# Revit family: RN 84234 Optiflex-Flowpress-Übergang
name_source: partatom
category: Rohrformteile
units: mm (PartAtom-declared; Revit-internal decimal feet)

## family parameters
Arbeitsebenenbasiert = Nein
Beim Laden mit Abzugskörper schneiden = Nein
Bemaßung runder Anschluss = Durchmesser verwenden
Gemeinsam genutzt = Nein
Immer vertikal = Ja
Teiletyp = Verbindung

## types (8) — shared parameters
1.010.00.2 Blattnummer der Richtlinie = 29
1.010.00.3 Ausgabedatum (Monat) der Richtlinie = 201308
1.010.00.4 Herstellername = R. Nussbaum AG
1.010.00.5 Revisionsdatum der Datei = 20190521
1.010.00.6 Webadresse des Herstellers = http://www.nussbaum.ch
1.100.00.4 Produktbezeichnung = Versorgung
1.110.00.2 Index = 5
1.110.00.4 Produktbezeichnung = Optiflex
1.960/3L.00.8 Link (URL) = https://www.nussbaum.ch
29.700.00.4 Produktname = Optiflex-Flowpress-Übergang, auf Optipress-Aquaplus, mit Einsteckende
29.700.00.5 Produktkennung = 2
29.700.00.6 Querschnittsform = 1
29.700.00.7 Nennweitensystem = DN
29.700.00.8 Nenndrucksystem = PN
29.710.02.4 Nenndruck = 10
29.710.02.5 max. zul. Überdruck [hPa] = 1000
29.710.02.7 max. zul. Dauer-Betriebsdruck [hPa] = 1000
29.710.02.9 max. zul. Dauer-Betriebstemperatur [°C] = 70
Connector Visibility = Nein
EnclosingSpace Visibility = Nein
Hersteller = R. Nussbaum AG
URL = https://www.nussbaum.ch

## per-type parameters (varying)
- DN=40: 1.800.00.3 TGA-Nummer=01900500000000000000000000000000000000000000000019000000000000000008; 1.800.00.4 Kommentarfeld=84234.28, Optiflex-Flowpress-Übergang, auf Optipress-Aquaplus, mit Einsteckende, DN=40, L=88; 1.810.00.3 Hersteller-Bestellnummer=84234.28; 1.810.00.4 DATANORM-Nummer=84234.28; 1.810.00.6 GTIN-Nummer=7612945744821; 29.710.02.10 Formstück-Gewicht [kg]=0.316; 29.710.02.3 Benennung=Optiflex-Flowpress-Übergang, auf Optipress-Aquaplus, mit Einsteckende, DN=40, L=88; CONNECTOR0_DIAMETER_dX_0r=40 mm; CONNECTOR0_dX_01=26 mm; CONNECTOR0_ref_dX=26 mm; CONNECTOR1_DIAMETER_dX_0r=40 mm; CONNECTOR1_dX_00=53 mm; CONNECTOR1_dX_01=89 mm; CONNECTOR1_ref_dX=89 mm; Modell=84234.28; R. Nussbaum AG 84234.21 de Visibility=Nein; R. Nussbaum AG 84234.22 de Visibility=Nein; R. Nussbaum AG 84234.23 de Visibility=Nein; R. Nussbaum AG 84234.24 de Visibility=Nein; R. Nussbaum AG 84234.25 de Visibility=Nein; R. Nussbaum AG 84234.26 de Visibility=Nein; R. Nussbaum AG 84234.27 de Visibility=Nein; R. Nussbaum AG 84234.28 de Visibility=Ja; Typenkommentare=Optiflex-Flowpress-Übergang DN=40
- DN=32: 1.800.00.3 TGA-Nummer=01900500000000000000000000000000000000000000000019000000000000000007; 1.800.00.4 Kommentarfeld=84234.27, Optiflex-Flowpress-Übergang, auf Optipress-Aquaplus, mit Einsteckende, DN=32, L=74; 1.810.00.3 Hersteller-Bestellnummer=84234.27; 1.810.00.4 DATANORM-Nummer=84234.27; 1.810.00.6 GTIN-Nummer=7612945730848; 29.710.02.10 Formstück-Gewicht [kg]=0.219; 29.710.02.3 Benennung=Optiflex-Flowpress-Übergang, auf Optipress-Aquaplus, mit Einsteckende, DN=32, L=74; CONNECTOR0_DIAMETER_dX_0r=32 mm; CONNECTOR0_dX_01=26 mm; CONNECTOR0_ref_dX=26 mm; CONNECTOR1_DIAMETER_dX_0r=32 mm; CONNECTOR1_dX_00=47 mm; CONNECTOR1_dX_01=73 mm; CONNECTOR1_ref_dX=73 mm; Modell=84234.27; R. Nussbaum AG 84234.21 de Visibility=Nein; R. Nussbaum AG 84234.22 de Visibility=Nein; R. Nussbaum AG 84234.23 de Visibility=Nein; R. Nussbaum AG 84234.24 de Visibility=Nein; R. Nussbaum AG 84234.25 de Visibility=Nein; R. Nussbaum AG 84234.26 de Visibility=Nein; R. Nussbaum AG 84234.27 de Visibility=Ja; R. Nussbaum AG 84234.28 de Visibility=Nein; Typenkommentare=Optiflex-Flowpress-Übergang DN=32
- DN=25: 1.800.00.3 TGA-Nummer=01900500000000000000000000000000000000000000000019000000000000000006; 1.800.00.4 Kommentarfeld=84234.26, Optiflex-Flowpress-Übergang, auf Optipress-Aquaplus, mit Einsteckende, DN=25, L=61; 1.810.00.3 Hersteller-Bestellnummer=84234.26; 1.810.00.4 DATANORM-Nummer=84234.26; 1.810.00.5 StLB-Nummer=346.474; 1.810.00.6 GTIN-Nummer=7612945730831; 29.710.02.10 Formstück-Gewicht [kg]=0.116; 29.710.02.3 Benennung=Optiflex-Flowpress-Übergang, auf Optipress-Aquaplus, mit Einsteckende, DN=25, L=61; CONNECTOR0_DIAMETER_dX_0r=25 mm  [stored 0.082021 ft]; CONNECTOR0_dX_01=20 mm; CONNECTOR0_ref_dX=20 mm; CONNECTOR1_DIAMETER_dX_0r=25 mm  [stored 0.082021 ft]; CONNECTOR1_dX_00=37 mm; CONNECTOR1_dX_01=61 mm; CONNECTOR1_ref_dX=61 mm; Modell=84234.26; R. Nussbaum AG 84234.21 de Visibility=Nein; R. Nussbaum AG 84234.22 de Visibility=Nein; R. Nussbaum AG 84234.23 de Visibility=Nein; R. Nussbaum AG 84234.24 de Visibility=Nein; R. Nussbaum AG 84234.25 de Visibility=Nein; R. Nussbaum AG 84234.26 de Visibility=Ja; R. Nussbaum AG 84234.27 de Visibility=Nein; R. Nussbaum AG 84234.28 de Visibility=Nein; Typenkommentare=Optiflex-Flowpress-Übergang DN=25
- DN=20: 1.800.00.3 TGA-Nummer=01900500000000000000000000000000000000000000000019000000000000000005; 1.800.00.4 Kommentarfeld=84234.25, Optiflex-Flowpress-Übergang, auf Optipress-Aquaplus, mit Einsteckende, DN=20, L=60; 1.810.00.3 Hersteller-Bestellnummer=84234.25; 1.810.00.4 DATANORM-Nummer=84234.25; 1.810.00.5 StLB-Nummer=346.473; 1.810.00.6 GTIN-Nummer=7612945730824; 29.710.02.10 Formstück-Gewicht [kg]=0.078; 29.710.02.3 Benennung=Optiflex-Flowpress-Übergang, auf Optipress-Aquaplus, mit Einsteckende, DN=20, L=60; CONNECTOR0_DIAMETER_dX_0r=20 mm; CONNECTOR0_dX_01=20 mm; CONNECTOR0_ref_dX=20 mm; CONNECTOR1_DIAMETER_dX_0r=20 mm; CONNECTOR1_dX_00=36 mm; CONNECTOR1_dX_01=60 mm; CONNECTOR1_ref_dX=60 mm; Modell=84234.25; R. Nussbaum AG 84234.21 de Visibility=Nein; R. Nussbaum AG 84234.22 de Visibility=Nein; R. Nussbaum AG 84234.23 de Visibility=Nein; R. Nussbaum AG 84234.24 de Visibility=Nein; R. Nussbaum AG 84234.25 de Visibility=Ja; R. Nussbaum AG 84234.26 de Visibility=Nein; R. Nussbaum AG 84234.27 de Visibility=Nein; R. Nussbaum AG 84234.28 de Visibility=Nein; Typenkommentare=Optiflex-Flowpress-Übergang DN=20
- DN=15x20: 1.800.00.3 TGA-Nummer=01900500000000000000000000000000000000000000000019000000000000000004; 1.800.00.4 Kommentarfeld=84234.24, Optiflex-Flowpress-Übergang, auf Optipress-Aquaplus, mit Einsteckende, DN=15x20, L=54; 1.810.00.3 Hersteller-Bestellnummer=84234.24; 1.810.00.4 DATANORM-Nummer=84234.24; 1.810.00.5 StLB-Nummer=346.472; 1.810.00.6 GTIN-Nummer=7612945730817; 29.710.02.10 Formstück-Gewicht [kg]=0.05; 29.710.02.3 Benennung=Optiflex-Flowpress-Übergang, auf Optipress-Aquaplus, mit Einsteckende, DN=15x20, L=54; CONNECTOR0_DIAMETER_dX_0r=15 mm; CONNECTOR0_dX_01=14 mm  [stored 0.0459318 ft]; CONNECTOR0_ref_dX=14 mm  [stored 0.0459318 ft]; CONNECTOR1_DIAMETER_dX_0r=20 mm; CONNECTOR1_dX_00=30 mm; CONNECTOR1_dX_01=54 mm; CONNECTOR1_ref_dX=54 mm; Modell=84234.24; R. Nussbaum AG 84234.21 de Visibility=Nein; R. Nussbaum AG 84234.22 de Visibility=Nein; R. Nussbaum AG 84234.23 de Visibility=Nein; R. Nussbaum AG 84234.24 de Visibility=Ja; R. Nussbaum AG 84234.25 de Visibility=Nein; R. Nussbaum AG 84234.26 de Visibility=Nein; R. Nussbaum AG 84234.27 de Visibility=Nein; R. Nussbaum AG 84234.28 de Visibility=Nein; Typenkommentare=Optiflex-Flowpress-Übergang DN=15x20
- DN=15: 1.800.00.3 TGA-Nummer=01900500000000000000000000000000000000000000000019000000000000000003; 1.800.00.4 Kommentarfeld=84234.23, Optiflex-Flowpress-Übergang, auf Optipress-Aquaplus, mit Einsteckende, DN=15, L=51; 1.810.00.3 Hersteller-Bestellnummer=84234.23; 1.810.00.4 DATANORM-Nummer=84234.23; 1.810.00.5 StLB-Nummer=346.472; 1.810.00.6 GTIN-Nummer=7612945730800; 29.710.02.10 Formstück-Gewicht [kg]=0.041; 29.710.02.3 Benennung=Optiflex-Flowpress-Übergang, auf Optipress-Aquaplus, mit Einsteckende, DN=15, L=51; CONNECTOR0_DIAMETER_dX_0r=15 mm; CONNECTOR0_dX_01=14 mm  [stored 0.0459318 ft]; CONNECTOR0_ref_dX=14 mm  [stored 0.0459318 ft]; CONNECTOR1_DIAMETER_dX_0r=15 mm; CONNECTOR1_dX_00=29 mm; CONNECTOR1_dX_01=51 mm; CONNECTOR1_ref_dX=51 mm; Modell=84234.23; R. Nussbaum AG 84234.21 de Visibility=Nein; R. Nussbaum AG 84234.22 de Visibility=Nein; R. Nussbaum AG 84234.23 de Visibility=Ja; R. Nussbaum AG 84234.24 de Visibility=Nein; R. Nussbaum AG 84234.25 de Visibility=Nein; R. Nussbaum AG 84234.26 de Visibility=Nein; R. Nussbaum AG 84234.27 de Visibility=Nein; R. Nussbaum AG 84234.28 de Visibility=Nein; Typenkommentare=Optiflex-Flowpress-Übergang DN=15
- DN=15x1: 1.800.00.3 TGA-Nummer=01900500000000000000000000000000000000000000000019000000000000000002; 1.800.00.4 Kommentarfeld=84234.22, Optiflex-Flowpress-Übergang, auf Optipress-Aquaplus, mit Einsteckende, DN=15x12, L=52; 1.810.00.3 Hersteller-Bestellnummer=84234.22; 1.810.00.4 DATANORM-Nummer=84234.22; 1.810.00.5 StLB-Nummer=346.471; 1.810.00.6 GTIN-Nummer=7612945730794; 29.710.02.10 Formstück-Gewicht [kg]=0.036; 29.710.02.3 Benennung=Optiflex-Flowpress-Übergang, auf Optipress-Aquaplus, mit Einsteckende, DN=15x12, L=52; CONNECTOR0_DIAMETER_dX_0r=12 mm  [stored 0.0393701 ft]; CONNECTOR0_dX_01=14 mm  [stored 0.0459318 ft]; CONNECTOR0_ref_dX=14 mm  [stored 0.0459318 ft]; CONNECTOR1_DIAMETER_dX_0r=15 mm; CONNECTOR1_dX_00=30 mm; CONNECTOR1_dX_01=52 mm; CONNECTOR1_ref_dX=52 mm; Modell=84234.22; R. Nussbaum AG 84234.21 de Visibility=Nein; R. Nussbaum AG 84234.22 de Visibility=Ja; R. Nussbaum AG 84234.23 de Visibility=Nein; R. Nussbaum AG 84234.24 de Visibility=Nein; R. Nussbaum AG 84234.25 de Visibility=Nein; R. Nussbaum AG 84234.26 de Visibility=Nein; R. Nussbaum AG 84234.27 de Visibility=Nein; R. Nussbaum AG 84234.28 de Visibility=Nein; Typenkommentare=Optiflex-Flowpress-Übergang DN=15x12
- DN=15x12: 1.800.00.3 TGA-Nummer=01900500000000000000000000000000000000000000000019000000000000000001; 1.800.00.4 Kommentarfeld=84234.21, Optiflex-Flowpress-Übergang, auf Optipress-Aquaplus, mit Einsteckende, DN=15x12, L=51; 1.810.00.3 Hersteller-Bestellnummer=84234.21; 1.810.00.4 DATANORM-Nummer=84234.21; 1.810.00.5 StLB-Nummer=346.471; 1.810.00.6 GTIN-Nummer=7612945730787; 29.710.02.10 Formstück-Gewicht [kg]=0.032; 29.710.02.3 Benennung=Optiflex-Flowpress-Übergang, auf Optipress-Aquaplus, mit Einsteckende, DN=15x12, L=51; CONNECTOR0_DIAMETER_dX_0r=12 mm  [stored 0.0393701 ft]; CONNECTOR0_dX_01=14 mm  [stored 0.0459318 ft]; CONNECTOR0_ref_dX=14 mm  [stored 0.0459318 ft]; CONNECTOR1_DIAMETER_dX_0r=12 mm  [stored 0.0393701 ft]; CONNECTOR1_dX_00=29 mm; CONNECTOR1_dX_01=51 mm; CONNECTOR1_ref_dX=51 mm; Modell=84234.21; R. Nussbaum AG 84234.21 de Visibility=Ja; R. Nussbaum AG 84234.22 de Visibility=Nein; R. Nussbaum AG 84234.23 de Visibility=Nein; R. Nussbaum AG 84234.24 de Visibility=Nein; R. Nussbaum AG 84234.25 de Visibility=Nein; R. Nussbaum AG 84234.26 de Visibility=Nein; R. Nussbaum AG 84234.27 de Visibility=Nein; R. Nussbaum AG 84234.28 de Visibility=Nein; Typenkommentare=Optiflex-Flowpress-Übergang DN=15x12

note: [stored X ft] marks values corroborated as IEEE doubles in the binary element streams (Revit-internal decimal feet)

## geometry (parser evidence)
native form markers: Sweep x1
no freeform markers — native parametric forms only
